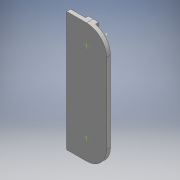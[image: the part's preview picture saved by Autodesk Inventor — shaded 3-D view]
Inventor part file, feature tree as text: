
AUTODESK INVENTOR PART (.ipt)
format: ipt  version: 2016 (Build 200138000, 138)  size: 107,008 bytes
history: native  units: mm
features: sketch x3, extrude x2, fillet x1
ambient origin geometry x8: Origin, YZ Plane, XZ Plane, XY Plane, X Axis, Y Axis, Z Axis, Center Point
bodies: Solid1 (feature_tree)
feature tree (6):
  extrude  "Extrusion1"  Depth=60.0mm
  extrude  "Extrusion2"  Depth=5.0mm
  fillet  "Fillet1"  Radius=1.5mm
  sketch  "Sketch3"  dims[d7=10.0mm]
  sketch  "Sketch1"  dims[d0=20.0mm d1=60.0mm]
  sketch  "Sketch2"  dims[d2=2.0mm d3=0.0mm d4=5.0mm d5=1.5mm d6=0.0mm]
